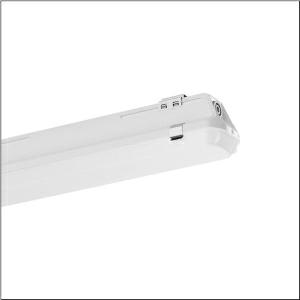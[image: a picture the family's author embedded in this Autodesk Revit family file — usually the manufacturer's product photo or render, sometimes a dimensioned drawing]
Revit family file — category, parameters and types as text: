
# Revit family: monsun_r__11_emergency_51fp20dp460hr_5229
name_source: partatom
category: Lighting Fixtures
units: mm (PartAtom-declared; Revit-internal decimal feet)

## family parameters
Cut with Voids When Loaded = No
Host = Face
Light Source = No
Part Type = Normal
Room Calculation Point = No
Round Connector Dimension = Use Diameter
Shared = No

## types (1)
- --- (1 x LED, 800 lm, 6.9 W, 4000K)
    Apparent Load = 7 VA
    CIE Flux Codes = 45 75 93 94 100
    Color Rendering = 80
    Color Temperature = 4000K
    Default Elevation = 1800 mm
    Description = Monsun® 11 emergency, damp-proof luminaire, chain hanger, primary optical cover: enclosure, of PC, light emission: direct distribution, primary light characteristic: symmetric, installation type: suspended mounting, surface-mounted, horizontal mounting, vertical mounting, LED, rated luminous flux: 5.450lm, luminous efficacy: 158lm/W, light colour: 840, colour temperature: 4000K, control gear: ECG DALI, with terminal, 5+2-pole, max. 2.5mm², mains connection: 220..240V, AC/DC, 0/50..60Hz, rated input power: 35W, changeover relay for equivalent power supply, AC/DC, 0/50..60Hz, luminaire housing, of glass-fibre reinforced polyester, uncoated, bright grey, incl. chain hanger, length: 1.590mm, width: 90mm, height: 88mm, clip for enclosure, of stainless steel (V2A), ceiling mounting element, of stainless steel (V2A), chain hanger, of stainless steel (V2A), protection rating (complete): IP66, insulation class (complete): insulation class I (protective earthing), certification: CE, UKCA, protection symbol: D, impact resistance: IK08, permissible operating ambient temperature: -25..+35°C, standard: EN 50419, EN 60598-2-1, EN 60598-2-22, no direct snow, no direct sun, no direct rain, for indoor or canopied outdoor use, corresponds to IFS (International Featured Standards) requirements for safety and quality in the food industry, contact your sales advisor before using the luminaires in applications with unclear chemical exposure, large temperature fluctuations or condensation-forming humidity, LABS conformity tested according to VDMA 24364:2018-05, packaging unit: 1 piece
    Height = 89 mm
    Lamp = 1 x LED
    Lamp Light Flux = 800 lm
    Lamp Power = 6.9 W
    Lamp count = 1
    Length = 1590 mm
    Luminous efficacy = 116 lm/W
    Manufacturer = Siteco
    ModVariant = No
    Model = 51FP20DP460HR
    Mounting Place = Ceiling
    Mounting Type = Surface mounted
    Number of Poles = 1
    OnlyDefault = Yes
    Power Factor = 1
    Product Name = Monsun® 11 emergency
    Product group = damp-proof luminaire
    ProductGroupID = 300
    Protection Class = Protection class I
    Protection Degree = IP 66
    RLX_Detail_Level = 1
    RLX_Emergency_Light_Flux = 0 lm
    RLX_Emergency_Type = 0
    RLX_Emergency_Type_DB = No
    RlxData = <blob elided: 92485 chars, md5=36311507>
    Socket = socket
    Standby Power = 0 W
    System Light Flux = 800 lm
    System Power = 7 W
    Type Comments = : equivalent power supply (DC)
    Type Image = l_1319650.jpg
    URL = http://relux.com
    VarID = @adj_171453
    Voltage = 0 V
    Weight = 0.00 kg
    Width = 90 mm

## geometry (parser evidence)
native form markers: Blend x4, Sweep x12
no freeform markers — native parametric forms only
